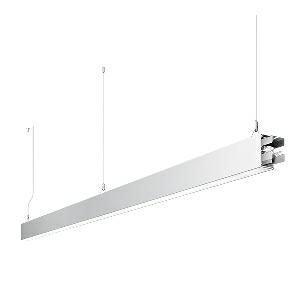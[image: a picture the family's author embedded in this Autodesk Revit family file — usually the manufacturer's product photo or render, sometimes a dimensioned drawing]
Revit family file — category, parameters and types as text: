
# Revit family: dotoo_line_-_dlp_3000_830_d_sta_00805810_c53b
name_source: partatom
category: Lighting Fixtures
units: mm (PartAtom-declared; Revit-internal decimal feet)

## family parameters
Cut with Voids When Loaded = No
Host = Face
Light Source = No
Part Type = Normal
Room Calculation Point = No
Round Connector Dimension = Use Diameter
Shared = No

## types (1)
- DOTOO.line - DLP 3000/830/D STA (1 x LED, 2650 lm, 3000K)
    Apparent Load = 26 VA
    Approval mark = CE
    CIE Flux Codes = 67 91 98 100 100
    Color Rendering = 80-89
    Color Temperature = 3000K
    Control Gear = Electronic ballast
    Default Elevation = 1800 mm
    Description = DLP 3000/830/D|Suspended luminaire|light source: LED|connected load: 220-240 V, 50/60 Hz|Power consumption: approx. 26 W|standby: approx. 0,15|luminous flux: 2650 lm|luminous efficacy: 101 lm/W|light distribution: Direct|direct ratio: approx. 100 %|colour temperature: Warm white, ca. 3000 K|color rendering index (CRI): >= 80|chromaticity tolerance:  3 SDCM|System of protection: IP 40|technology: Continuously dimmable|luminaire body|material: Sectional aluminium|colour: White|lamp cover: Acrylic (PMMA), Clear|mains lead: 2,0 m With free stranded wires|Fastening: Steel cable 0.3 - 0.7 m|glare control: Conical prismatic screen|luminance(L65): <= 3000 cd/m|unified glare rating(4H 8H): <=  19|special features: DALI Load 1x, TouchDIM - dimming via standard switch, Through-wired, up to 18 m on one mains connection, Flicker-free, Suitable as emergency lighting, Start luminaire with mains connection, Mechanical and electrical connection of the individual modules without tools|
    Frequency = 50 Hz
    Height = 110 mm
    Lamp = 1 x LED
    Lamp Light Flux = 2650 lm
    Lamp count = 1
    Length = 2250 mm
    Luminous efficacy = 102 lm/W
    Manufacturer = Waldmann
    ModVariant = No
    Model = 00805810
    Mounting Place = Ceiling
    Mounting Type = Pendant
    Number of Poles = 1
    OnlyDefault = Yes
    Power Factor = 1
    Product Name = DOTOO.line - DLP 3000/830/D STA
    Product group = Suspended luminaire
    ProductGroupID = 9
    Protection Class = Protection class I
    Protection Degree = IP 40
    RLX_Detail_Level = 1
    RLX_Emergency_Light_Flux = 0 lm
    RLX_Emergency_Type = 0
    RLX_Emergency_Type_DB = No
    RlxData = <blob elided: 23149 chars, md5=63ff311a>
    Socket = socket
    Standby Power = 0 W
    System Light Flux = 2650 lm
    System Power = 26 W
    Type Comments = Product without accessories
    Type Image = 113313000-00692603.jpg
    URL = http://relux.com
    VarID = ---
    Voltage = 230 V
    Voltage Range = 220-240 V
    Weight = 0.00 kg
    Width = 60 mm  [stored 0.19685 ft]

note: [stored X ft] marks values corroborated as IEEE doubles in the binary element streams (Revit-internal decimal feet)

## geometry (parser evidence)
native form markers: Blend x4, Sweep x13
no freeform markers — native parametric forms only
